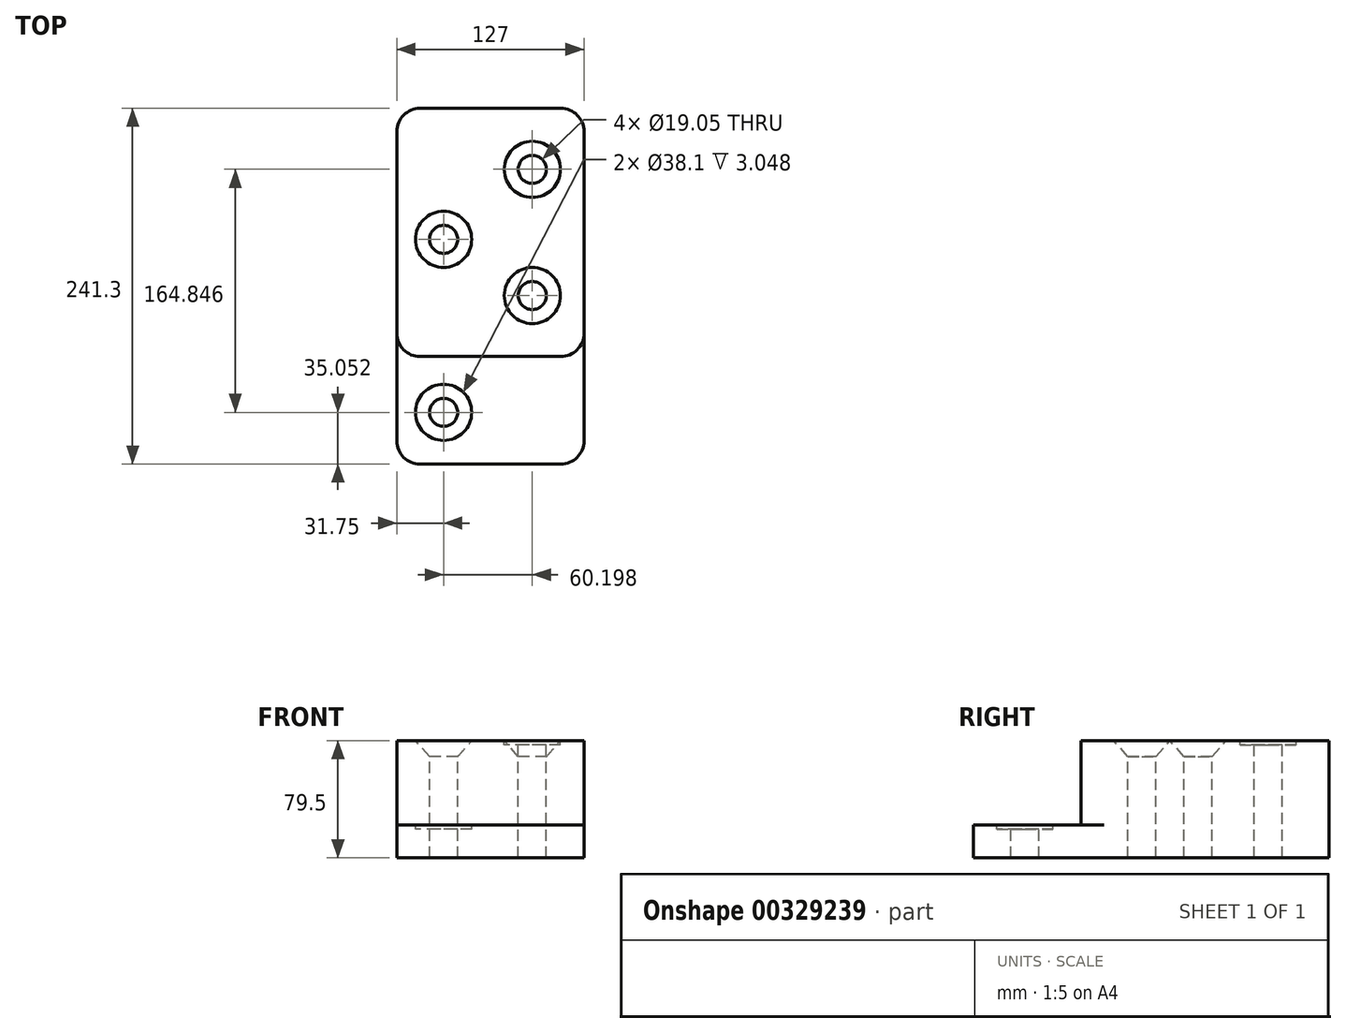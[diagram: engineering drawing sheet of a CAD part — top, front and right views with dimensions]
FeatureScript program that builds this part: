
annotation { "Feature Type Name" : "Feature", "Feature Type Description" : "" }
export const myFeature = defineFeature(function(context is Context, id is Id, definition is map)
    precondition{}
    {
        {
            var Q0;
            Q0=qCreatedBy(makeId("Top.planeOp"),FACE);
            var sketch = newSketch(context, id + "F0", { "sketchPlane" : qUnion([Q0])});
            skLineSegment(sketch, "E0", {"start": v(0, 0) * mm, "end": v(127, 0) * mm});
            skLineSegment(sketch, "E1", {"start": v(127, 0) * mm, "end": v(127, -168.4) * mm});
            skLineSegment(sketch, "E2", {"start": v(127, -168.4) * mm, "end": v(0, -168.4) * mm});
            skLineSegment(sketch, "E3", {"start": v(0, -168.4) * mm, "end": v(0, 0) * mm});
            skLineSegment(sketch, "E4", {"start": v(127, -168.4) * mm, "end": v(127, -241.3) * mm});
            skLineSegment(sketch, "E5", {"start": v(127, -241.3) * mm, "end": v(0, -241.3) * mm});
            skLineSegment(sketch, "E6", {"start": v(0, -241.3) * mm, "end": v(0, -168.4) * mm});
            skPoint(sketch, "E7", {"position": v(31.75, -88.9) * mm});
            skPoint(sketch, "E8", {"position": v(91.95, -41.4) * mm});
            skPoint(sketch, "E9", {"position": v(91.95, -127) * mm});
            skPoint(sketch, "E10", {"position": v(31.75, -206.25) * mm});
            skSolve(sketch);
        }
        {
            var Q0;
            Q0=makeQuery(id+"F0.imprint","IMPRINT",FACE,{"disambiguationData":[TD([[makeQuery(id+"F0.imprint","IMPRINT",EDGE,{"derivedFrom":sQuery(id+"F0.wireOp",EDGE,"E0")}),-1.0]])]});
            extrude(context, id + "F1", {"entities" : qUnion([Q0]), "oppositeDirection" : true, "depth" : 79.5 * mm});
        }
        {
            var Q0;
            Q0=makeQuery(id+"F0.imprint","IMPRINT",FACE,{"disambiguationData":[TD([[makeQuery(id+"F0.imprint","IMPRINT",EDGE,{"derivedFrom":sQuery(id+"F0.wireOp",EDGE,"E2")}),1.0]])]});
            extrude(context, id + "F2", {"entities" : qUnion([Q0]), "operationType" : NewBodyOperationType.ADD, "oppositeDirection" : true, "depth" : 79.5 * mm, "hasSecondDirection" : true, "secondDirectionOppositeDirection" : true, "secondDirectionDepth" : 57.15 * mm});
        }
        {
            var Q0;
            Q0=makeQuery(id+"F1.opExtrude","SWEPT_EDGE",EDGE,{"disambiguationData":[OSD([sQuery(id+"F0.wireOp",EDGE,"E1"),sQuery(id+"F0.wireOp",EDGE,"E2"),sQuery(id+"F0.wireOp",EDGE,"E4")])]});
            var Q1;
            Q1=makeQuery(id+"F2.opExtrude","SWEPT_EDGE",EDGE,{"disambiguationData":[OSD([sQuery(id+"F0.wireOp",EDGE,"E4"),sQuery(id+"F0.wireOp",EDGE,"E5")])]});
            var Q2;
            Q2=makeQuery(id+"F2.opExtrude","SWEPT_EDGE",EDGE,{"disambiguationData":[OSD([sQuery(id+"F0.wireOp",EDGE,"E5"),sQuery(id+"F0.wireOp",EDGE,"E6")])]});
            var Q3;
            Q3=makeQuery(id+"F1.opExtrude","SWEPT_EDGE",EDGE,{"disambiguationData":[OSD([sQuery(id+"F0.wireOp",EDGE,"E2"),sQuery(id+"F0.wireOp",EDGE,"E3"),sQuery(id+"F0.wireOp",EDGE,"E6")])]});
            var Q4;
            Q4=makeQuery(id+"F1.opExtrude","SWEPT_EDGE",EDGE,{"disambiguationData":[OSD([sQuery(id+"F0.wireOp",EDGE,"E0"),sQuery(id+"F0.wireOp",EDGE,"E1")])]});
            var Q5;
            Q5=makeQuery(id+"F1.opExtrude","SWEPT_EDGE",EDGE,{"disambiguationData":[OSD([sQuery(id+"F0.wireOp",EDGE,"E0"),sQuery(id+"F0.wireOp",EDGE,"E3")])]});
            fillet(context, id + "F3", {"entities" : qUnion([Q0, Q1, Q2, Q3, Q4, Q5]), "radius" : 15.75 * mm, "tangentPropagation" : true, "allowEdgeOverflow" : false});
        }
        {
            var Q0;
            Q0=sQuery(id+"F0.wireOp",VERTEX,"E8");
            var Q1;
            Q1=sQuery(id+"F0.wireOp",VERTEX,"E10");
            var Q2;
            Q2=makeQuery(id+"F1.opExtrude","SWEPT_BODY",BODY,{"disambiguationData":[OSD([sQuery(id+"F0.wireOp",EDGE,"E0"),sQuery(id+"F0.wireOp",EDGE,"E1"),sQuery(id+"F0.wireOp",EDGE,"E2"),sQuery(id+"F0.wireOp",EDGE,"E3")])]});
            hole(context, id + "F4", {"style" : HoleStyle.C_BORE, "endStyle" : HoleEndStyle.THROUGH, "holeDiameter" : 19.05 * mm, "cBoreDiameter" : 38.1 * mm, "cBoreDepth" : 3.05 * mm, "tappedDepth" : 12.7 * mm, "tapClearance" : 3, "locations" : qUnion([Q0, Q1]), "scope" : qUnion([Q2])});
        }
        {
            var Q0;
            Q0=sQuery(id+"F0.wireOp",VERTEX,"E7");
            var Q1;
            Q1=sQuery(id+"F0.wireOp",VERTEX,"E9");
            var Q2;
            Q2=makeQuery(id+"F1.opExtrude","SWEPT_BODY",BODY,{"disambiguationData":[OSD([sQuery(id+"F0.wireOp",EDGE,"E0"),sQuery(id+"F0.wireOp",EDGE,"E1"),sQuery(id+"F0.wireOp",EDGE,"E2"),sQuery(id+"F0.wireOp",EDGE,"E3")])]});
            hole(context, id + "F5", {"style" : HoleStyle.C_SINK, "endStyle" : HoleEndStyle.THROUGH, "holeDiameter" : 19.05 * mm, "cSinkDiameter" : 38.1 * mm, "cSinkAngle" : 82 * degree, "tappedDepth" : 12.7 * mm, "tapClearance" : 3, "locations" : qUnion([Q0, Q1]), "scope" : qUnion([Q2])});
        }
    });
